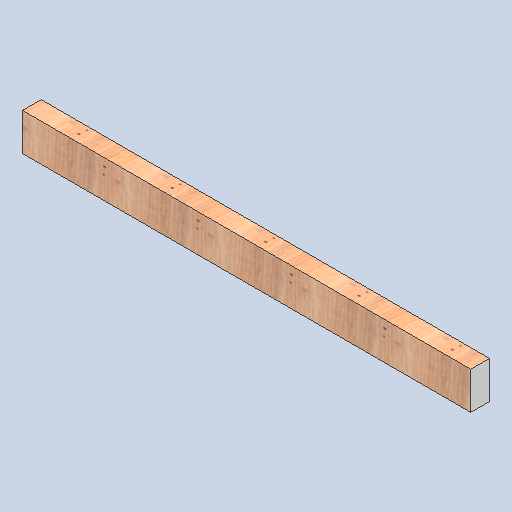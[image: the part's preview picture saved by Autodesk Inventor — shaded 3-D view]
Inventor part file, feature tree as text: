
AUTODESK INVENTOR PART (.ipt)
format: ipt  version: 2025 (Build 290162000, 162)  size: 159,744 bytes
history: native  units: in
note: dims shown in document units (in); Inventor stores cm internally (conversion verified against a paired STEP export)
features: extrude x2, sketch x2
ambient origin geometry x8: Origin, YZ Plane, XZ Plane, XY Plane, X Axis, Y Axis, Z Axis, Center Point
bodies: Solid1 (feature_tree)
feature tree (4):
  extrude  "Extrusion1"  Depth=4.0in
  extrude  "Extrusion2"  Depth=48.0in TaperAngle=0.0deg
  sketch  "Sketch1"  dims[d0=96.0in d1=4.0in]
  sketch  "Sketch2"  dims[d2=2.0in d3=0.0in d4=48.0in d5=0.0in]
